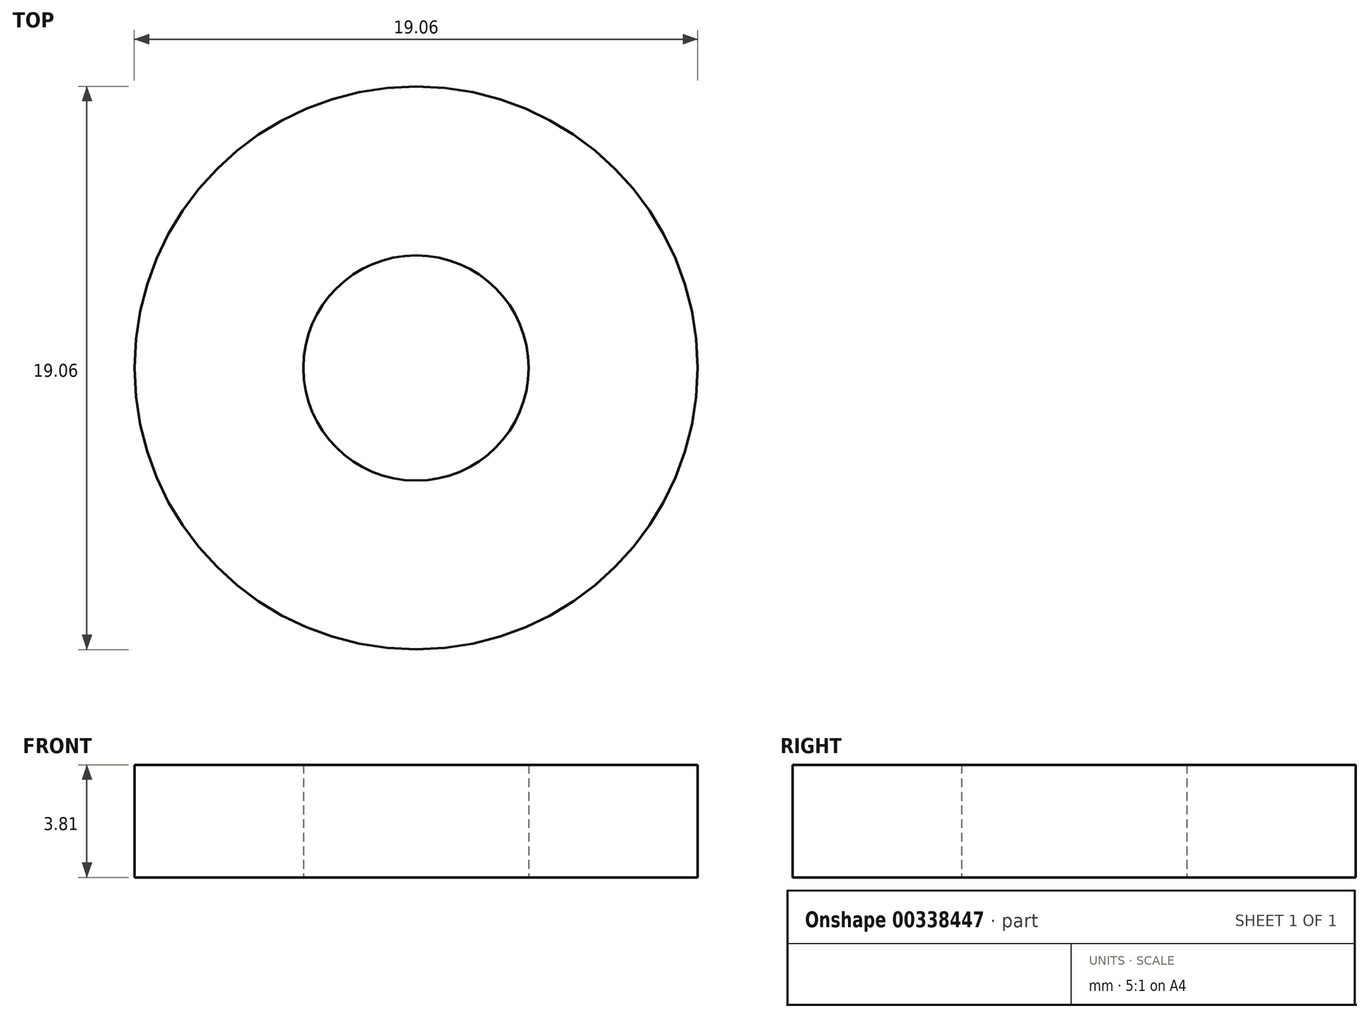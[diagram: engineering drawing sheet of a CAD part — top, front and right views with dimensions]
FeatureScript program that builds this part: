
annotation { "Feature Type Name" : "Feature", "Feature Type Description" : "" }
export const myFeature = defineFeature(function(context is Context, id is Id, definition is map)
    precondition{}
    {
        {
            var Q0;
            Q0=qCreatedBy(makeId("Top.planeOp"),FACE);
            var sketch = newSketch(context, id + "F0", { "sketchPlane" : qUnion([Q0])});
            skCircle(sketch, "E0", {"center": v(0, 0) * mm, "radius": 9.53 * mm});
            skCircle(sketch, "E1", {"center": v(0, 0) * mm, "radius": 3.81 * mm});
            skSolve(sketch);
        }
        {
            var Q0;
            Q0=makeQuery(id+"F0.imprint","IMPRINT",FACE,{"disambiguationData":[TD([[makeQuery(id+"F0.imprint","IMPRINT",EDGE,{"derivedFrom":sQuery(id+"F0.wireOp",EDGE,"E0")}),1.0]])]});
            extrude(context, id + "F1", {"entities" : qUnion([Q0]), "depth" : 3.8 * mm});
        }
    });
